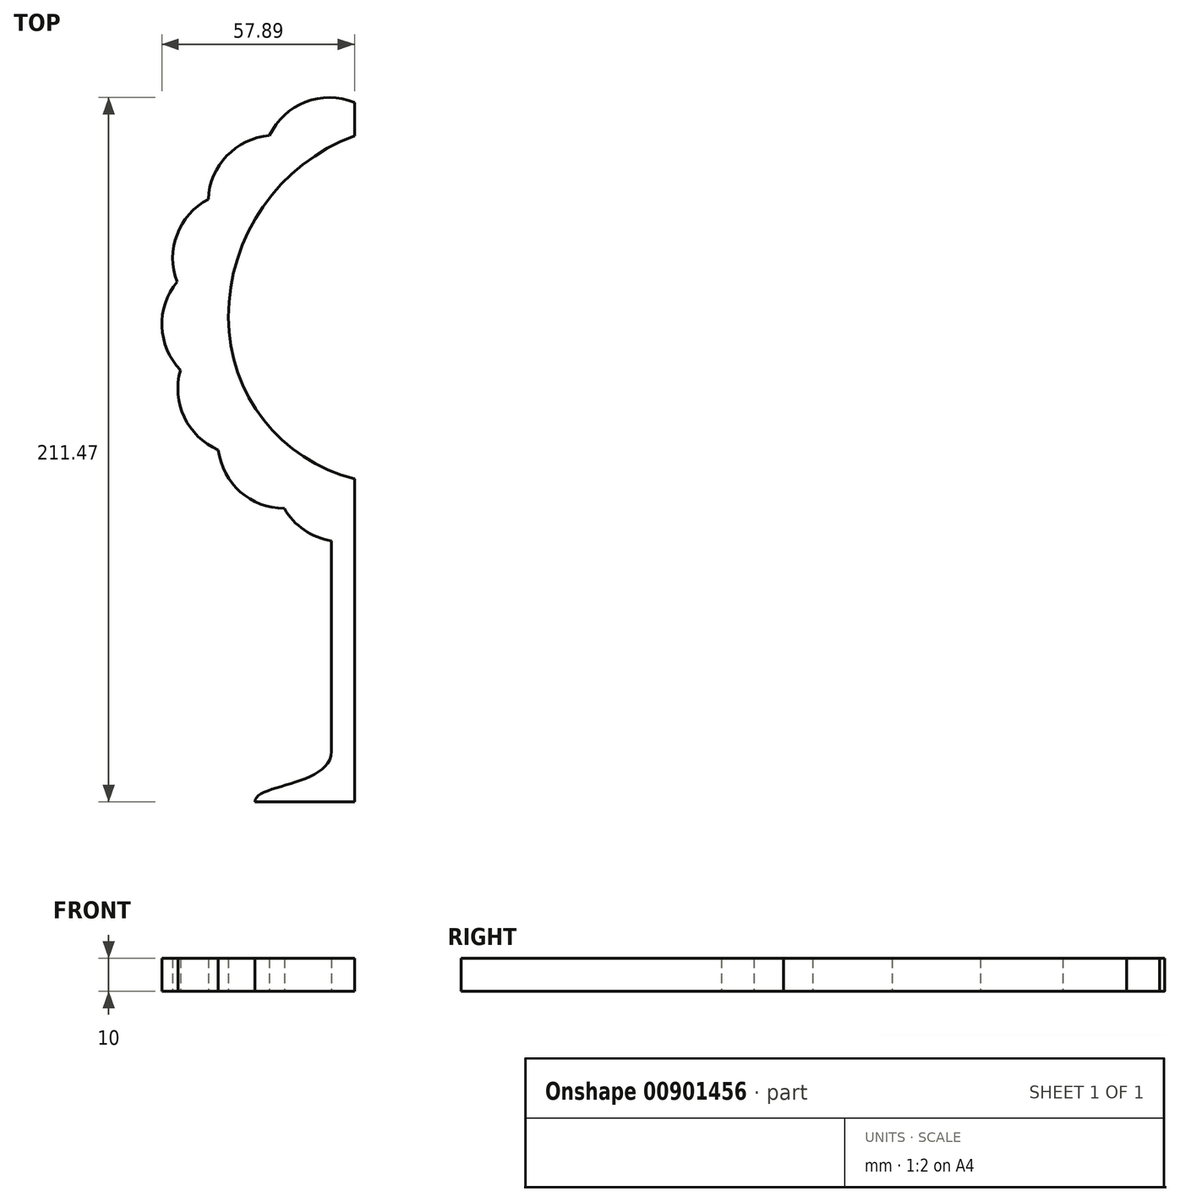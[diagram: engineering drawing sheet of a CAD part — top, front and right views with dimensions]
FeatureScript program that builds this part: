
annotation { "Feature Type Name" : "Feature", "Feature Type Description" : "" }
export const myFeature = defineFeature(function(context is Context, id is Id, definition is map)
    precondition{}
    {
        {
            var Q0;
            Q0=qCreatedBy(makeId("Top.planeOp"),FACE);
            var sketch = newSketch(context, id + "F0", { "sketchPlane" : qUnion([Q0])});
            skPoint(sketch, "E0.center.orphan", {"position": v(0, 50) * mm});
            skArc(sketch, "E1", {"start": v(-12.07, 64.53) * mm, "mid": v(-26.85, 64.64) * mm, "end": v(-37.66, 54.58) * mm});
            skArc(sketch, "E2", {"start": v(-37.66, 54.58) * mm, "mid": v(-50.48, 48.5) * mm, "end": v(-56.04, 35.45) * mm});
            skArc(sketch, "E3", {"start": v(-56.04, 35.45) * mm, "mid": v(-65.45, 24.83) * mm, "end": v(-65.45, 10.65) * mm});
            skArc(sketch, "E4", {"start": v(-65.45, 10.65) * mm, "mid": v(-69.94, -2.8) * mm, "end": v(-64.39, -15.85) * mm});
            skArc(sketch, "E5", {"start": v(-53.02, -39.82) * mm, "mid": v(-46.44, -52.38) * mm, "end": v(-33.17, -57.42) * mm});
            skArc(sketch, "E6", {"start": v(-33.17, -57.42) * mm, "mid": v(-27.22, -63.88) * mm, "end": v(-19.07, -67.16) * mm});
            skArc(sketch, "E7.trimOffspring", {"start": v(-64.39, -15.85) * mm, "mid": v(-63.25, -30) * mm, "end": v(-53.02, -39.82) * mm});
            skLineSegment(sketch, "E8", {"start": v(-12.07, 64.53) * mm, "end": v(-12.07, 54.53) * mm});
            skArc(sketch, "E9.trimOffspring", {"start": v(-50, 0) * mm, "mid": v(-39.4, -30.8) * mm, "end": v(-12.07, -48.52) * mm});
            skArc(sketch, "E10", {"start": v(-50, 0) * mm, "mid": v(-39.59, 33.21) * mm, "end": v(-12.07, 54.53) * mm});
            skLineSegment(sketch, "E11", {"start": v(-12.07, -145.47) * mm, "end": v(-42.07, -145.47) * mm});
            skLineSegment(sketch, "E12", {"start": v(-19.07, -67.16) * mm, "end": v(-19.07, -130.47) * mm});
            skLineSegment(sketch, "E13", {"start": v(-12.07, -145.47) * mm, "end": v(-12.07, -48.52) * mm});
            skFitSpline(sketch, "E14", {"points": [v(-19.07, -130.47) * mm, v(-42.07, -145.47) * mm], "startDerivative": vector(0.17, -30.58) * mm, "endDerivative": vector(-0.25, -15.99) * mm});
            skSolve(sketch);
        }
        {
            var Q0;
            Q0=makeQuery(id+"F0.imprint","IMPRINT",FACE,{"disambiguationData":[TD([[makeQuery(id+"F0.imprint","IMPRINT",EDGE,{"derivedFrom":sQuery(id+"F0.wireOp",EDGE,"E1")}),1.0]])]});
            extrude(context, id + "F1", {"entities" : qUnion([Q0]), "depth" : 10 * mm, "offsetDistance" : 25 * mm});
        }
    });
